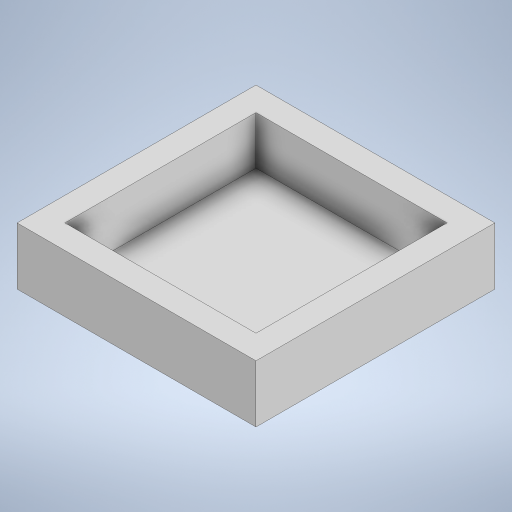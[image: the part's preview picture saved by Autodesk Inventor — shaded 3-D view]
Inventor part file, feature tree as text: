
AUTODESK INVENTOR PART (.ipt)
format: ipt  version: 2024.3 (Build 283343000, 343)  size: 217,088 bytes
history: native  units: in
note: dims shown in document units (in); Inventor stores cm internally (conversion verified against a paired STEP export)
features: extrude x2, sketch x2
ambient origin geometry x8: Origin, YZ Plane, XZ Plane, XY Plane, X Axis, Y Axis, Z Axis, Center Point
bodies: Solid1 (feature_tree)
feature tree (4):
  extrude  "Extrusion1"  Depth=2.3622in TaperAngle=0.0deg
  extrude  "Extrusion2"  Depth=1.9843in TaperAngle=0.0deg
  sketch  "Sketch1"  dims[d0=9.8425in d1=2.3622in d2=0.0in]
  sketch  "Sketch2"  dims[d3=7.874in d4=1.9843in d5=0.0in]
